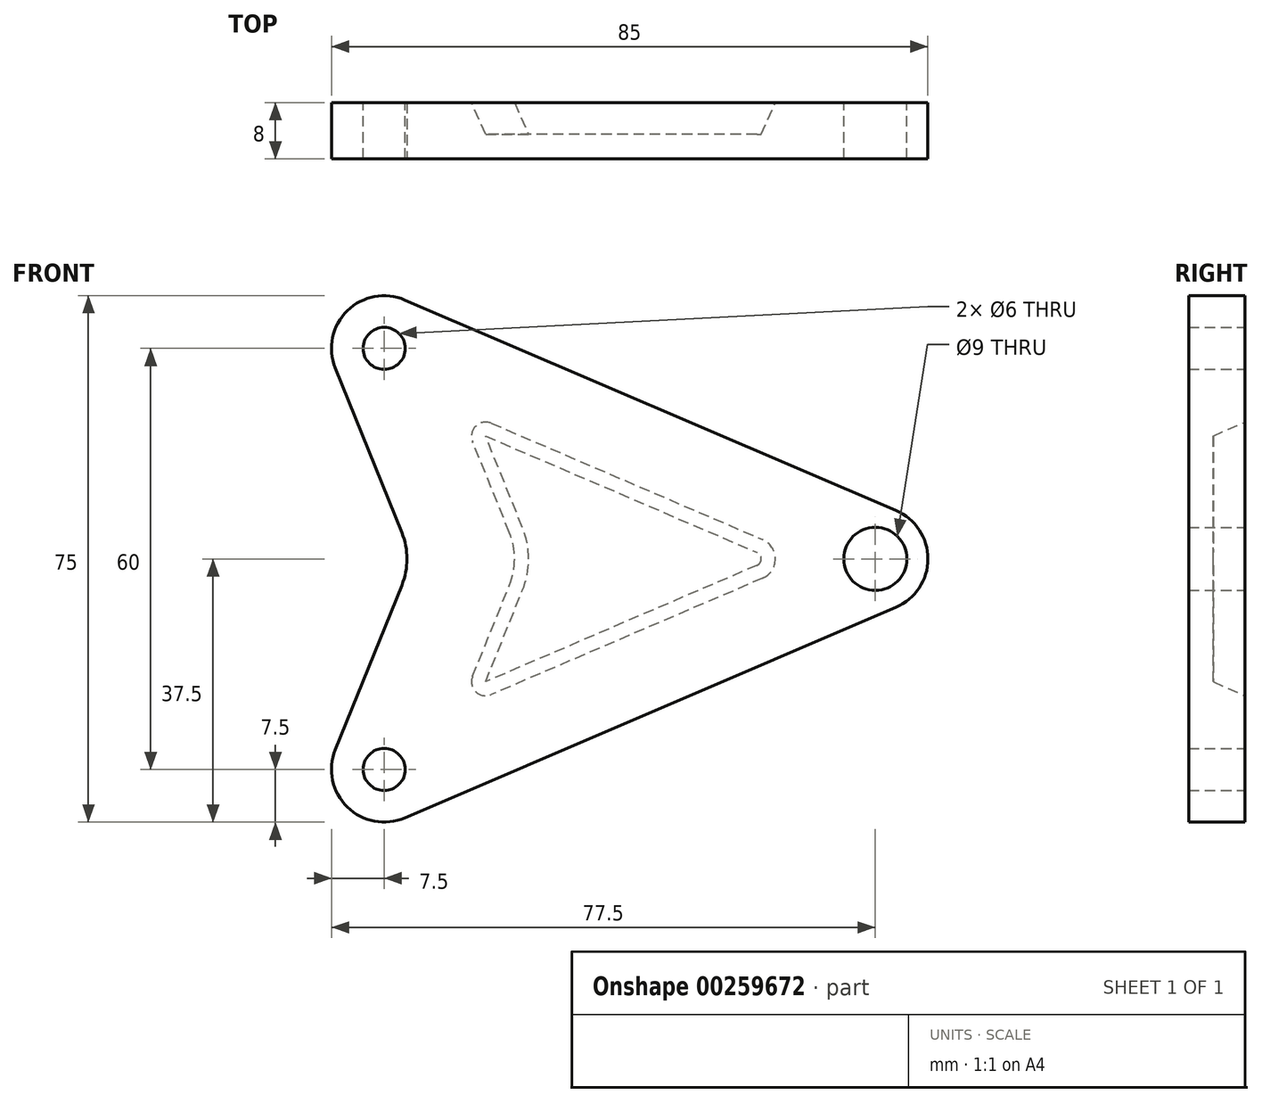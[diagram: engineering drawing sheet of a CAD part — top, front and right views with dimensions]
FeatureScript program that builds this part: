
annotation { "Feature Type Name" : "Feature", "Feature Type Description" : "" }
export const myFeature = defineFeature(function(context is Context, id is Id, definition is map)
    precondition{}
    {
        {
            var Q0;
            Q0=qCreatedBy(makeId("Front.planeOp"),FACE);
            var sketch = newSketch(context, id + "F0", { "sketchPlane" : qUnion([Q0])});
            skCircle(sketch, "E0", {"center": v(0, 30) * mm, "radius": 3 * mm});
            skCircle(sketch, "E1", {"center": v(0, -30) * mm, "radius": 3 * mm});
            skCircle(sketch, "E2", {"center": v(70, 0) * mm, "radius": 4.5 * mm});
            skCircle(sketch, "E3", {"center": v(0, 30) * mm, "radius": 7.5 * mm});
            skCircle(sketch, "E4", {"center": v(70, 0) * mm, "radius": 7.5 * mm});
            skCircle(sketch, "E5", {"center": v(0, -30) * mm, "radius": 7.5 * mm});
            skLineSegment(sketch, "E6", {"start": v(72.95, -6.9) * mm, "end": v(2.95, -36.9) * mm});
            skLineSegment(sketch, "E7", {"start": v(2.95, -36.9) * mm, "end": v(2.95, -36.9) * mm});
            skLineSegment(sketch, "E8", {"start": v(2.95, 36.9) * mm, "end": v(72.95, 6.9) * mm});
            skLineSegment(sketch, "E9", {"start": v(-6.95, 27.2) * mm, "end": v(4.03, 0) * mm});
            skLineSegment(sketch, "E10", {"start": v(4.03, 0) * mm, "end": v(-6.95, -27.2) * mm});
            skSolve(sketch);
        }
        {
            var Q0;
            Q0 = qSketchRegion(id + "F0", true);
            extrude(context, id + "F1", {"entities" : qUnion([Q0]), "depth" : 8 * mm});
        }
        {
            var Q0;
            Q0=makeQuery(id+"F1.opExtrude","SWEPT_EDGE",EDGE,{"disambiguationData":[OSD([sQuery(id+"F0.wireOp",EDGE,"E9"),sQuery(id+"F0.wireOp",EDGE,"E10")])]});
            fillet(context, id + "F2", {"entities" : qUnion([Q0]), "radius" : 10 * mm, "tangentPropagation" : true, "allowEdgeOverflow" : false});
        }
        {
            var Q0;
            Q0=qCreatedBy(makeId("Front.planeOp"),FACE);
            var sketch = newSketch(context, id + "F3", { "sketchPlane" : qUnion([Q0])});
            skLineSegment(sketch, "E11", {"start": v(17.85, 3.75) * mm, "end": v(12.6, 16.75) * mm});
            skLineSegment(sketch, "E12", {"start": v(15.24, 19.34) * mm, "end": v(53.92, 2.76) * mm});
            skLineSegment(sketch, "E13", {"start": v(53.92, -2.76) * mm, "end": v(15.24, -19.34) * mm});
            skLineSegment(sketch, "E14", {"start": v(12.6, -16.75) * mm, "end": v(17.85, -3.75) * mm});
            skPoint(sketch, "E15.visualSharp", {"position": v(19.37, 0) * mm});
            skArc(sketch, "E15.filletArc", {"start": v(17.85, -3.75) * mm, "mid": v(18.58, 0) * mm, "end": v(17.85, 3.75) * mm});
            skPoint(sketch, "E16.visualSharp", {"position": v(10.78, 21.25) * mm});
            skArc(sketch, "E16.filletArc", {"start": v(15.24, 19.34) * mm, "mid": v(13.05, 18.93) * mm, "end": v(12.6, 16.75) * mm});
            skPoint(sketch, "E17.visualSharp", {"position": v(10.78, -21.25) * mm});
            skArc(sketch, "E17.filletArc", {"start": v(12.6, -16.75) * mm, "mid": v(13.05, -18.93) * mm, "end": v(15.24, -19.34) * mm});
            skPoint(sketch, "E18.visualSharp", {"position": v(60.36, 0) * mm});
            skArc(sketch, "E18.filletArc", {"start": v(53.92, -2.76) * mm, "mid": v(55.74, 0) * mm, "end": v(53.92, 2.76) * mm});
            skSolve(sketch);
        }
        {
            var Q0;
            Q0 = qSketchRegion(id + "F3", true);
            extrude(context, id + "F4", {"entities" : qUnion([Q0]), "operationType" : NewBodyOperationType.REMOVE, "depth" : 4.5 * mm, "offsetDistance" : 25 * mm});
        }
        {
            var Q0;
            Q0=makeQuery(id+"F4.boolean.opBoolean","COPY",EDGE,{"derivedFrom":makeQuery(id+"F4.opExtrude","CAP_EDGE",EDGE,{"disambiguationData":[OSD([sQuery(id+"F3.wireOp",EDGE,"E12")])],"isStart":false})});
            chamfer(context, id + "F5", {"entities" : qUnion([Q0]), "chamferType" : ChamferType.TWO_OFFSETS, "width1" : 2 * mm, "oppositeDirection" : false, "width2" : 4.5 * mm, "tangentPropagation" : true});
        }
    });
